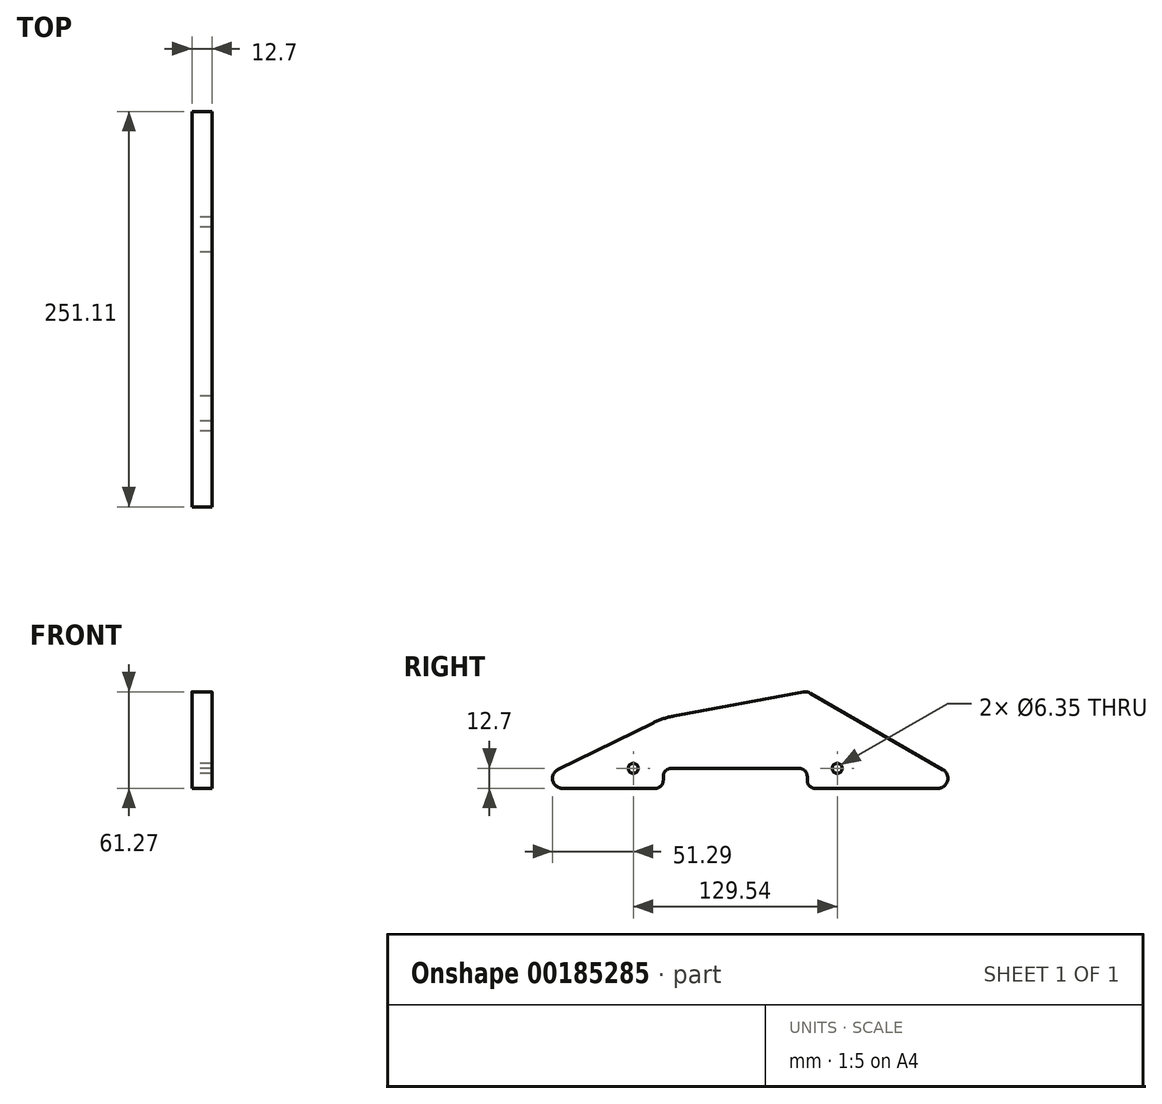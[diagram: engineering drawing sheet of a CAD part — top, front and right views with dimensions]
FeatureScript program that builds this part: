
annotation { "Feature Type Name" : "Feature", "Feature Type Description" : "" }
export const myFeature = defineFeature(function(context is Context, id is Id, definition is map)
    precondition{}
    {
        {
            var Q0;
            Q0=qCreatedBy(makeId("Right.planeOp"),FACE);
            var sketch = newSketch(context, id + "F0", { "sketchPlane" : qUnion([Q0])});
            skPoint(sketch, "E0.orphan", {"position": v(0, 0) * mm});
            skLineSegment(sketch, "E1", {"start": v(91.44, 0) * mm, "end": v(0, 0) * mm});
            skLineSegment(sketch, "E2", {"start": v(184.9, 60.42) * mm, "end": v(269.04, 11.85) * mm});
            skLineSegment(sketch, "E3", {"start": v(27.45, 0) * mm, "end": v(86.36, 0) * mm, "construction": true});
            skLineSegment(sketch, "E4", {"start": v(24.66, 12.05) * mm, "end": v(85.2, 41.65) * mm});
            skLineSegment(sketch, "E5", {"start": v(91.44, 5.08) * mm, "end": v(91.44, 7.62) * mm});
            skLineSegment(sketch, "E6", {"start": v(96.52, 12.7) * mm, "end": v(177.8, 12.7) * mm});
            skLineSegment(sketch, "E7", {"start": v(265.86, 0) * mm, "end": v(187.96, 0) * mm});
            skLineSegment(sketch, "E8", {"start": v(182.88, 5.08) * mm, "end": v(182.88, 7.62) * mm});
            skPoint(sketch, "E9", {"position": v(137.16, 12.7) * mm});
            skPoint(sketch, "E10.newPointA", {"position": v(91.44, 0) * mm});
            skArc(sketch, "E10.filletArc", {"start": v(86.36, 0) * mm, "mid": v(89.95, 1.49) * mm, "end": v(91.44, 5.08) * mm});
            skArc(sketch, "E11.filletArc", {"start": v(24.66, 12.05) * mm, "mid": v(21.26, 4.92) * mm, "end": v(27.45, 0) * mm});
            skPoint(sketch, "E12.visualSharp", {"position": v(91.44, 44.7) * mm});
            skPoint(sketch, "E13.visualSharp", {"position": v(91.44, 12.7) * mm});
            skArc(sketch, "E13.filletArc", {"start": v(96.52, 12.7) * mm, "mid": v(92.93, 11.21) * mm, "end": v(91.44, 7.62) * mm});
            skPoint(sketch, "E14.visualSharp", {"position": v(182.88, 12.7) * mm});
            skArc(sketch, "E14.filletArc", {"start": v(182.88, 7.62) * mm, "mid": v(181.4, 11.21) * mm, "end": v(177.8, 12.7) * mm});
            skPoint(sketch, "E15.visualSharp", {"position": v(182.88, 61.6) * mm});
            skPoint(sketch, "E16.visualSharp", {"position": v(182.88, 0) * mm});
            skArc(sketch, "E16.filletArc", {"start": v(182.88, 5.08) * mm, "mid": v(184.37, 1.49) * mm, "end": v(187.96, 0) * mm});
            skPoint(sketch, "E17.visualSharp", {"position": v(289.56, 0) * mm});
            skArc(sketch, "E17.filletArc", {"start": v(265.86, 0) * mm, "mid": v(272, 4.7) * mm, "end": v(269.04, 11.85) * mm});
            skLineSegment(sketch, "E18", {"start": v(91.44, 5.08) * mm, "end": v(91.44, 44.7) * mm, "construction": true});
            skPoint(sketch, "E19", {"position": v(72.4, 12.7) * mm});
            skCircle(sketch, "E20", {"center": v(72.4, 12.7) * mm, "radius": 3.18 * mm});
            skPoint(sketch, "E21", {"position": v(201.93, 12.7) * mm});
            skLineSegment(sketch, "E22", {"start": v(182.88, 5.08) * mm, "end": v(182.88, 61.6) * mm, "construction": true});
            skCircle(sketch, "E23", {"center": v(201.93, 12.7) * mm, "radius": 3.18 * mm});
            skLineSegment(sketch, "E24", {"start": v(98.28, 45.97) * mm, "end": v(180.58, 61.17) * mm});
            skArc(sketch, "E25.filletArc", {"start": v(98.28, 45.97) * mm, "mid": v(91.59, 44.25) * mm, "end": v(85.2, 41.65) * mm});
            skArc(sketch, "E26.filletArc", {"start": v(184.9, 60.42) * mm, "mid": v(182.8, 61.18) * mm, "end": v(180.58, 61.17) * mm});
            skSolve(sketch);
        }
        {
            var Q0;
            Q0 = qSketchRegion(id + "F0", true);
            extrude(context, id + "F1", {"entities" : qUnion([Q0]), "depth" : 12.7 * mm});
        }
    });
